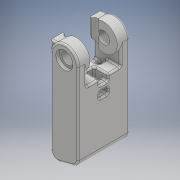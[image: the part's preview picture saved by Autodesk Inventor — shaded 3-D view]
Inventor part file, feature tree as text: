
AUTODESK INVENTOR PART (.ipt)
format: ipt  version: 2018 (Build 220112000, 112)  size: 653,312 bytes
history: native  units: mm
features: extrude x18, sketch x18, other x5, fillet x5
ambient origin geometry x8: Origin, YZ Plane, XZ Plane, XY Plane, X Axis, Y Axis, Z Axis, Center Point
bodies: Body1 (feature_tree)
feature tree (46):
  other  "Sólido1"
  extrude  "Extrusión1"  Depth=50.0mm
  extrude  "Extrusión2"  Depth=5.0mm
  extrude  "Extrusión3"  Depth=15.0mm
  extrude  "Extrusión4"  Depth=5.0mm TaperAngle=0.0deg
  extrude  "Extrusión5"  Depth=10.0mm
  extrude  "Extrusión6"  Depth=2.5mm
  extrude  "Extrusión7"  Depth=10.0mm TaperAngle=0.0deg
  extrude  "Extrusión8"  Depth=30.0mm TaperAngle=0.0deg
  extrude  "Extrusión9"  Depth=30.0mm TaperAngle=0.0deg
  other  "Edición directa1"
  extrude  "Extrusión10"  Depth=2.0mm TaperAngle=0.0deg
  extrude  "Extrusión11"  [1 undecoded]
  extrude  "Extrusión12"  Depth=2.0mm
  fillet  "Empalme1"  Radius=2.0mm
  fillet  "Empalme2"  Radius=2.0mm
  fillet  "Empalme3"  Radius=2.0mm
  fillet  "Empalme4"  Radius=2.5mm
  other  "Edición directa2"
  extrude  "Extrusión13"  Depth=3.0mm
  extrude  "Extrusión14"  Depth=4.0mm
  extrude  "Extrusión15"  Depth=4.0mm
  extrude  "Extrusión16"  Depth=20.0mm TaperAngle=0.0deg
  extrude  "Extrusión17"  Depth=1.0mm
  fillet  "Empalme5"  Radius=1.0mm
  extrude  "Extrusión18"  Depth=2.0mm TaperAngle=0.0deg
  sketch  "Boceto1"  dims[d0=30.0mm d1=50.0mm]
  sketch  "Boceto2"  dims[d2=20.0mm d3=0.0mm d4=5.0mm]
  sketch  "Boceto4"  dims[d7=20.0mm d8=0.0mm d9=15.0mm]
  sketch  "Boceto5"  dims[d10=5.0mm d11=0.0mm d12=5.0mm d13=0.0mm]
  sketch  "Boceto6"  dims[d14=5.0mm d15=10.0mm]
  sketch  "Boceto7"  dims[d16=5.0mm d17=2.5mm]
  sketch  "Boceto8"  dims[d18=5.0mm d19=10.0mm d20=0.0mm]
  sketch  "Boceto9"  dims[d21=5.0mm d22=30.0mm d23=0.0mm]
  sketch  "Boceto10"  dims[d24=7.0mm d25=30.0mm d26=0.0mm]
  sketch  "Boceto11"  dims[d27=10.0mm d28=2.0mm d29=0.0mm]
  sketch  "Boceto12"  dims[d30=2.0mm d31=0.0mm d32=-2.0mm]
  sketch  "Boceto13"  dims[d33=2.0mm d34=2.0mm d35=2.0mm d36=2.0mm d37=2.0mm d38=0.0mm d43=2.5mm]
  sketch  "Boceto14"  dims[d44=0.5mm d45=3.0mm]
  sketch  "Boceto15"  dims[d46=5.0mm d47=0.0mm d48=4.0mm]
  sketch  "Boceto16"  dims[d49=3.0mm d50=4.0mm]
  sketch  "Boceto17"  dims[d51=3.0mm d52=20.0mm d53=0.0mm]
  sketch  "Boceto18"  dims[d54=4.0mm d55=1.0mm d56=1.0mm]
  sketch  "Boceto19"  dims[d57=1.0mm d58=0.0mm d59=0.0mm d60=3.0mm d61=4.0mm d62=0.0mm d63=4.0mm d64=0.0mm d65=3.0mm d66=7.5mm d67=7.5mm d68=4.0mm d69=4.0mm d70=20.0mm d71=0.0mm d76=14.0mm d77=2.0mm d78=23.0mm d79=7.0mm d80=0.0mm d81=0.0mm d82=7.5mm d83=3.0mm d84=7.5mm d85=8.0mm d86=4.0mm d87=0.0mm d88=0.0mm d89=1.0mm d90=20.0mm d91=0.0mm]
  other  "Tamaño1"
  other  "Desplazar1"
note: 1 required parameter value undecoded (feature->parameter linkage not recoverable at this tier; creation-order binding heuristic only, values carry confidence <= 0.55)
